# Revit family: IS_Eurovit+_V3027_BIM_NL
name_source: partatom
category: Plumbing Fixtures
revit_build: Autodesk Revit MEP 2014 (Build: 20130308_1515(x64)
units: mm (PartAtom-declared; Revit-internal decimal feet)

## types (1)
- V302701 - EUROVIT WASTAFEL 60 CM, RECHTHOEKIG
    Accessories = www.idealstandardnederland.nl
    AreaUnits = millimeters
    Assembly Code = C1030200
    AssetType = Vast
    BIMObjectName = ISI_IdealStandard_Wall-HungWashBasins_V302701
    BarCode = 8595095902671
    Brand = Ideal Standard
    CWFU = 0
    CodePerformance = DIN EN 14688 CL 25, DIN EN 31
    Color = Wit
    ConnectionType = Sanitair
    Cost = 0 $
    Default Elevation = 850 mm  [stored 2.78871 ft]
    Description = Eurovit Plus wastafel 600 mm van keramiek met waterlijst. 1 kraangat midden doorgestoken, 2 kraangaten links en rechts voorgestoken. Met overloop. Bevestiging met 2 schroeven M10 x 140 mm (K710767). Exclusief bevestigingsmateriaal.
    DrainSize = 0 mm  [stored 0 ft]
    DurationUnit = jaar
    ECA = No
    ExpectedLife = 25
    Features = Wastafel 600 mm van keramiek met waterlijst. 1 kraangat midden doorgestoken, 2 kraangaten links en rechts voorgestoken. Met overloop. Bevestiging met 2 schroeven M10 x 140 mm (K710767). Exclusief bevestigingsmateriaal.
    Finish = Wit
    HWFU = 0
    IfcExportAs = IfcSanitaryType
    IfcExportType = WASHHANDBASIN
    InstallationInstructions = http://www.idealstandardnederland.nl
    LinearUnits = millimeters
    ManufacturerURL = www.idealstandardnederland.nl
    Material = Keramiek
    Model = V302701
    ModelNumber = V302701
    ModelReference = Eurovit Plus wastafel 600 mm van keramiek met waterlijst. 1 kraangat midden doorgestoken, 2 kraangaten links en rechts voorgestoken. Met overloop. Bevestiging met 2 schroeven M10 x 140 mm (K710767). Exclusief bevestigingsmateriaal.
    NBSDescription = Wall hung wash basins
    NBSReference = 45-35-70/369
    Name = Wall-HungWashBasins_V302701_IdealStandard
    NettWeight = 17.64 kg
    NominalDepth = 0 mm  [stored 0 ft]
    NominalHeight = 187 mm
    NominalLength = 460 mm
    NominalWidth = 600 mm
    ProductInformation = http://www.idealstandardnederland.nl
    Shape = Rechthoekig
    Size = 600 x 460 x 187 mm
    Space = Internal
    URL = www.idealstandardnederland.nl
    Uniclass2015Code = Pr_40_20_96_96
    Uniclass2015Title = Wall-hung wash basins
    Uniclass2015Version = Products v1.1
    Version = 1
    VolumeUnits = liter
    WFU = 0
    WRAS = No
    WarrantyDescription = Fabrieksgarantie
    WarrantyDurationParts = 5
    WarrantyDurationUnit = jaar
    WashHandBasinMounting = Wandhangend
    WashHandBasinType = Wastafel
    WaterEfficientProduct = No

note: [stored X ft] marks values corroborated as IEEE doubles in the binary element streams (Revit-internal decimal feet)

## geometry (parser evidence)
native form markers: Sweep x2
no freeform markers — native parametric forms only
